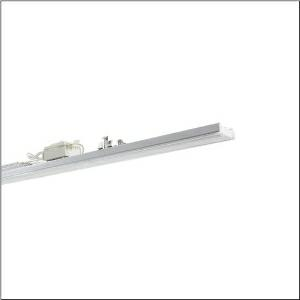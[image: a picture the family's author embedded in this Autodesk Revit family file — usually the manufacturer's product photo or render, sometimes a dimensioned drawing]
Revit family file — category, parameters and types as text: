
# Revit family: licross_r__21_recessed_mo_52te187n485g_b208
name_source: partatom
category: Lighting Fixtures
units: mm (PartAtom-declared; Revit-internal decimal feet)

## family parameters
Cut with Voids When Loaded = No
Host = Face
Light Source = No
Part Type = Normal
Room Calculation Point = No
Round Connector Dimension = Use Diameter
Shared = No

## types (1)
- Licross® 21 Recessed MO (1 x LED, 8570 lm, 47.9 W, 4000K)
    Apparent Load = 48 VA
    CIE Flux Codes = 79 95 99 100 100
    Color Rendering = 80
    Color Temperature = 4000K
    Default Elevation = 1800 mm
    Description = Licross® 21 Recessed MO, luminaire insert, of sheet steel, galvanised, coil coated, white, length: 1.500mm, width: 66mm, height: 67mm, LED rated luminous flux: 8.570lm, light colour: 840, control gear: ON/OFF, with plug, 3-pole, with phase selection, mains connection: 220..240V, AC, 50/60Hz, rated input power: 48W, internal wiring halogen-free, primary light control with lens, of plastic, primary optical cover: cover, of PMMA, light emission: direct distribution, primary light characteristic: symmetric, protection rating (complete): IP54, insulation class (complete): insulation class I (protective earthing), certification: CE, ENEC, VDE, UKCA, protection symbol: D if used in an environment with non-conductive dust loads with corresponding accessories, impact resistance: IK06, permissible ambient temperature for indoor applications: -35..+40°C, corresponds to IFS (International Featured Standards) requirements for safety and quality in the food industry, reducing of maximum allowable ambient temperature of 5°C with ceiling mounting, LABS conformity tested according to VDMA 24364:2018-05, packaging unit: 1 piece
    Height = 58 mm
    Lamp = 1 x LED
    Lamp Light Flux = 8570 lm
    Lamp Power = 47.9 W
    Lamp count = 1
    Length = 1500 mm
    Luminous efficacy = 179 lm/W
    Manufacturer = Siteco
    ModVariant = No
    Model = 52TE187N485G
    Mounting Place = Ceiling
    Mounting Type = Pendant
    Number of Poles = 1
    OnlyDefault = Yes
    Power Factor = 1
    Product Name = Licross® 21 Recessed MO
    Product group = luminaire insert | ceiling pendant
    ProductGroupID = 902
    Protection Class = Protection class I
    Protection Degree = IP 54
    RLX_Detail_Level = 1
    RLX_Emergency_Light_Flux = 0 lm
    RLX_Emergency_Type = 0
    RLX_Emergency_Type_DB = No
    RlxData = <blob elided: 20957 chars, md5=4f7dda1f>
    Socket = socket
    Standby Power = 0 W
    System Light Flux = 8570 lm
    System Power = 48 W
    Type Comments = Product without accessories
    Type Image = l_1296930.jpg
    URL = http://relux.com
    VarID = ---
    Voltage = 0 V
    Weight = 0.00 kg
    Width = 66 mm

## geometry (parser evidence)
native form markers: Blend x4, Sweep x11
no freeform markers — native parametric forms only
